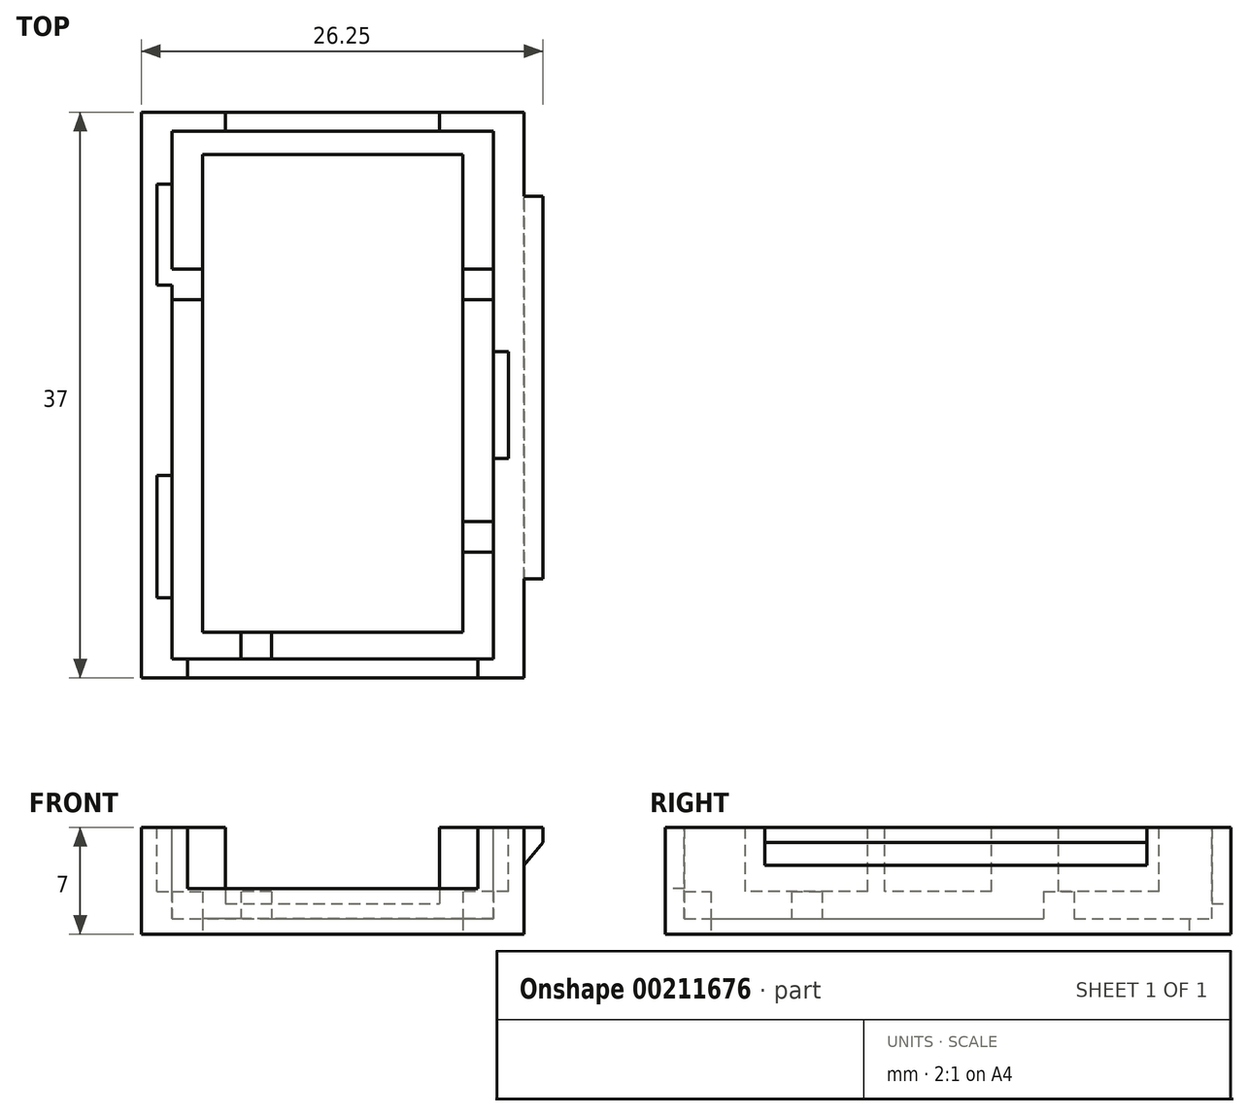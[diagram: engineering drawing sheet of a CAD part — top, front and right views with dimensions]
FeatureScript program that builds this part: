
annotation { "Feature Type Name" : "Feature", "Feature Type Description" : "" }
export const myFeature = defineFeature(function(context is Context, id is Id, definition is map)
    precondition{}
    {
        {
            var Q0;
            Q0=qCreatedBy(makeId("Top.planeOp"),FACE);
            var sketch = newSketch(context, id + "F0", { "sketchPlane" : qUnion([Q0])});
            skLineSegment(sketch, "E0", {"start": v(0, 0) * mm, "end": v(65.42, 0) * mm, "construction": true});
            skLineSegment(sketch, "E1", {"start": v(0, 0) * mm, "end": v(0, 57) * mm, "construction": true});
            skLineSegment(sketch, "E2.bottom", {"start": v(11, 17.5) * mm, "end": v(-11, 17.5) * mm, "construction": true});
            skLineSegment(sketch, "E2.top", {"start": v(11, -17.5) * mm, "end": v(-11, -17.5) * mm, "construction": true});
            skLineSegment(sketch, "E2.left", {"start": v(11, 17.5) * mm, "end": v(11, -17.5) * mm, "construction": true});
            skLineSegment(sketch, "E2.right", {"start": v(-11, 17.5) * mm, "end": v(-11, -17.5) * mm, "construction": true});
            skPoint(sketch, "E2.middle", {"position": v(0, 0) * mm});
            skPoint(sketch, "E3.orphan", {"position": v(0, -17.5) * mm});
            skLineSegment(sketch, "E4.bottom", {"start": v(12.5, 19) * mm, "end": v(-12.5, 19) * mm});
            skLineSegment(sketch, "E4.top", {"start": v(12.5, -19) * mm, "end": v(-12.5, -19) * mm});
            skLineSegment(sketch, "E4.left", {"start": v(12.5, 19) * mm, "end": v(12.5, -19) * mm});
            skLineSegment(sketch, "E4.right", {"start": v(-12.5, 19) * mm, "end": v(-12.5, -19) * mm});
            skSolve(sketch);
        }
        {
            var Q0;
            Q0=makeQuery(id+"F0.imprint","IMPRINT",FACE,{"disambiguationData":[TD([[makeQuery(id+"F0.imprint","IMPRINT",EDGE,{"derivedFrom":sQuery(id+"F0.wireOp",EDGE,"E4.bottom")}),1.0]])]});
            extrude(context, id + "F1", {"entities" : qUnion([Q0]), "depth" : 7 * mm});
        }
        {
            var Q0;
            Q0=makeQuery(id+"F1.opExtrude","CAP_FACE",FACE,{"disambiguationData":[OSD([sQuery(id+"F0.wireOp",EDGE,"E4.bottom"),sQuery(id+"F0.wireOp",EDGE,"E4.top"),sQuery(id+"F0.wireOp",EDGE,"E4.left"),sQuery(id+"F0.wireOp",EDGE,"E4.right")])],"isStart":false});
            var sketch = newSketch(context, id + "F2", { "sketchPlane" : qUnion([Q0])});
            skLineSegment(sketch, "E5.bottom", {"start": v(-10.5, -17.75) * mm, "end": v(10.5, -17.75) * mm});
            skLineSegment(sketch, "E5.top", {"start": v(-10.5, 16.75) * mm, "end": v(10.5, 16.75) * mm});
            skLineSegment(sketch, "E5.left", {"start": v(-10.5, -17.75) * mm, "end": v(-10.5, 16.75) * mm});
            skLineSegment(sketch, "E5.right", {"start": v(10.5, -17.75) * mm, "end": v(10.5, 16.75) * mm});
            skSolve(sketch);
        }
        {
            var Q0;
            Q0=qSketchRegion(id+"F2",true);
            extrude(context, id + "F3", {"entities" : qUnion([Q0]), "operationType" : NewBodyOperationType.REMOVE, "oppositeDirection" : true, "depth" : 6 * mm});
        }
        {
            var Q0;
            Q0=makeQuery(id+"F3.boolean.opBoolean","COPY",FACE,{"derivedFrom":makeQuery(id+"F3.opExtrude","CAP_FACE",FACE,{"disambiguationData":[OSD([sQuery(id+"F2.wireOp",EDGE,"E5.bottom"),sQuery(id+"F2.wireOp",EDGE,"E5.top"),sQuery(id+"F2.wireOp",EDGE,"E5.left"),sQuery(id+"F2.wireOp",EDGE,"E5.right")])],"isStart":false})});
            var sketch = newSketch(context, id + "F4", { "sketchPlane" : qUnion([Q0])});
            skLineSegment(sketch, "E6.bottom", {"start": v(-10.5, 5.75) * mm, "end": v(-8.5, 5.75) * mm});
            skLineSegment(sketch, "E6.top", {"start": v(-10.5, 7.75) * mm, "end": v(-8.5, 7.75) * mm});
            skLineSegment(sketch, "E6.left", {"start": v(-10.5, 7.75) * mm, "end": v(-10.5, 5.75) * mm});
            skLineSegment(sketch, "E6.right", {"start": v(-8.5, 7.75) * mm, "end": v(-8.5, 5.75) * mm});
            skLineSegment(sketch, "E7.MirrorCS", {"start": v(10.5, 5.75) * mm, "end": v(8.5, 5.75) * mm});
            skLineSegment(sketch, "E8.MirrorCS", {"start": v(8.5, 7.75) * mm, "end": v(8.5, 5.75) * mm});
            skLineSegment(sketch, "E9.MirrorCS", {"start": v(10.5, 7.75) * mm, "end": v(8.5, 7.75) * mm});
            skLineSegment(sketch, "E10.MirrorCS", {"start": v(10.5, 7.75) * mm, "end": v(10.5, 5.75) * mm});
            skLineSegment(sketch, "E11.bottom", {"start": v(10.5, -10.75) * mm, "end": v(8.5, -10.75) * mm});
            skLineSegment(sketch, "E11.top", {"start": v(10.5, -8.75) * mm, "end": v(8.5, -8.75) * mm});
            skLineSegment(sketch, "E11.left", {"start": v(10.5, -10.75) * mm, "end": v(10.5, -8.75) * mm});
            skLineSegment(sketch, "E11.right", {"start": v(8.5, -10.75) * mm, "end": v(8.5, -8.75) * mm});
            skLineSegment(sketch, "E12.bottom", {"start": v(-6, -18) * mm, "end": v(-4, -18) * mm});
            skLineSegment(sketch, "E12.top", {"start": v(-6, -16) * mm, "end": v(-4, -16) * mm});
            skLineSegment(sketch, "E12.left", {"start": v(-6, -18) * mm, "end": v(-6, -16) * mm});
            skLineSegment(sketch, "E12.right", {"start": v(-4, -18) * mm, "end": v(-4, -16) * mm});
            skSolve(sketch);
        }
        {
            var Q0;
            Q0=qSketchRegion(id+"F4",true);
            extrude(context, id + "F5", {"entities" : qUnion([Q0]), "operationType" : NewBodyOperationType.ADD, "depth" : 1.8 * mm});
        }
        {
            var Q0;
            Q0=qCreatedBy(makeId("Top.planeOp"),FACE);
            var sketch = newSketch(context, id + "F6", { "sketchPlane" : qUnion([Q0])});
            skLineSegment(sketch, "E13.bottom", {"start": v(-8.5, 15.25) * mm, "end": v(8.5, 15.25) * mm});
            skLineSegment(sketch, "E13.left", {"start": v(-8.5, 15.25) * mm, "end": v(-8.5, -16) * mm});
            skLineSegment(sketch, "E14.top", {"start": v(-8.5, -16) * mm, "end": v(8.5, -16) * mm});
            skLineSegment(sketch, "E14.right", {"start": v(8.5, 15.25) * mm, "end": v(8.5, -16) * mm});
            skSolve(sketch);
        }
        {
            var Q0;
            Q0=qSketchRegion(id+"F6",true);
            extrude(context, id + "F7", {"entities" : qUnion([Q0]), "operationType" : NewBodyOperationType.REMOVE, "endBound" : BoundingType.THROUGH_ALL, "depth" : 25 * mm});
        }
        {
            var Q0;
            Q0=makeQuery(id+"F1.opExtrude","CAP_FACE",FACE,{"disambiguationData":[OSD([sQuery(id+"F0.wireOp",EDGE,"E4.bottom"),sQuery(id+"F0.wireOp",EDGE,"E4.top"),sQuery(id+"F0.wireOp",EDGE,"E4.left"),sQuery(id+"F0.wireOp",EDGE,"E4.right")])],"isStart":false});
            var sketch = newSketch(context, id + "F8", { "sketchPlane" : qUnion([Q0])});
            skLineSegment(sketch, "E15.bottom", {"start": v(-10.47, 6.7) * mm, "end": v(-11.47, 6.7) * mm});
            skLineSegment(sketch, "E15.top", {"start": v(-10.47, 13.3) * mm, "end": v(-11.47, 13.3) * mm});
            skLineSegment(sketch, "E15.left", {"start": v(-10.47, 6.7) * mm, "end": v(-10.47, 13.3) * mm});
            skLineSegment(sketch, "E15.right", {"start": v(-11.47, 6.7) * mm, "end": v(-11.47, 13.3) * mm});
            skLineSegment(sketch, "E16.bottom", {"start": v(10.5, 2.35) * mm, "end": v(11.5, 2.35) * mm});
            skLineSegment(sketch, "E16.top", {"start": v(10.5, -4.65) * mm, "end": v(11.5, -4.65) * mm});
            skLineSegment(sketch, "E16.left", {"start": v(10.5, 2.35) * mm, "end": v(10.5, -4.65) * mm});
            skLineSegment(sketch, "E16.right", {"start": v(11.5, 2.35) * mm, "end": v(11.5, -4.65) * mm});
            skLineSegment(sketch, "E17.bottom", {"start": v(-10.5, -13.75) * mm, "end": v(-11.47, -13.75) * mm});
            skLineSegment(sketch, "E17.top", {"start": v(-10.5, -5.75) * mm, "end": v(-11.47, -5.75) * mm});
            skLineSegment(sketch, "E17.left", {"start": v(-10.5, -13.75) * mm, "end": v(-10.5, -5.75) * mm});
            skLineSegment(sketch, "E17.right", {"start": v(-11.47, -13.75) * mm, "end": v(-11.47, -5.75) * mm});
            skSolve(sketch);
        }
        {
            var Q0;
            {var subQ0=sQuery(id+"F8.wireOp",EDGE,"E15.bottom");Q0=makeQuery(id+"F8.imprint","IMPRINT",FACE,{"disambiguationData":[TD([[makeQuery(id+"F8.imprint","IMPRINT",EDGE,{"derivedFrom":subQ0}),-1.0]])]});}
            var Q1;
            {var subQ0=sQuery(id+"F8.wireOp",EDGE,"E15.top");Q1=makeQuery(id+"F8.imprint","IMPRINT",FACE,{"disambiguationData":[TD([[makeQuery(id+"F8.imprint","IMPRINT",EDGE,{"derivedFrom":subQ0}),1.0]])]});}
            var Q2;
            Q2=makeQuery(id+"F8.imprint","IMPRINT",FACE,{"disambiguationData":[TD([[makeQuery(id+"F8.imprint","IMPRINT",EDGE,{"derivedFrom":sQuery(id+"F8.wireOp",EDGE,"E16.bottom")}),-1.0]])]});
            var Q3;
            {var subQ0=sQuery(id+"F8.wireOp",EDGE,"lNjhLBkX-aFZr-f505-E5Ee-j5UPzdD6XMNG.bottom");Q3=makeQuery(id+"F8.imprint","IMPRINT",FACE,{"disambiguationData":[TD([[makeQuery(id+"F8.imprint","IMPRINT",EDGE,{"derivedFrom":subQ0}),1.0]])]});}
            var Q4;
            {var subQ0=sQuery(id+"F8.wireOp",EDGE,"lNjhLBkX-aFZr-f505-E5Ee-j5UPzdD6XMNG.top");Q4=makeQuery(id+"F8.imprint","IMPRINT",FACE,{"disambiguationData":[TD([[makeQuery(id+"F8.imprint","IMPRINT",EDGE,{"derivedFrom":subQ0}),-1.0]])]});}
            var Q5;
            Q5=makeQuery(id+"F8.imprint","IMPRINT",FACE,{"disambiguationData":[TD([[makeQuery(id+"F8.imprint","IMPRINT",EDGE,{"derivedFrom":sQuery(id+"F8.wireOp",EDGE,"E17.bottom")}),-1.0]])]});
            var Q6;
            Q6=makeQuery(id+"F5.opExtrude","CAP_FACE",FACE,{"disambiguationData":[OSD([sQuery(id+"F4.wireOp",EDGE,"E6.bottom"),sQuery(id+"F4.wireOp",EDGE,"E6.top"),sQuery(id+"F4.wireOp",EDGE,"E6.left"),sQuery(id+"F4.wireOp",EDGE,"E6.right")])],"isStart":false});
            extrude(context, id + "F9", {"entities" : qUnion([Q0, Q1, Q2, Q3, Q4, Q5]), "operationType" : NewBodyOperationType.REMOVE, "endBound" : BoundingType.UP_TO_SURFACE, "oppositeDirection" : true, "endBoundEntityFace" : qUnion([Q6]), "depth" : 3 * mm});
        }
        {
            var Q0;
            {var subQ10=sQuery(id+"F4.wireOp",EDGE,"E6.bottom");Q0=makeQuery(id+"F4.imprint","IMPRINT",FACE,{"disambiguationData":[TD([[makeQuery(id+"F4.imprint","IMPRINT",EDGE,{"derivedFrom":subQ10}),-1.0]])]});}
            cPlane(context, id + "F10", {"entities" : qUnion([Q0]), "cplaneType" : CPlaneType.OFFSET, "offset" : 1 * mm, "width" : 150 * mm, "height" : 150 * mm});
        }
        {
            var Q0;
            Q0=qCreatedBy(id+"F10.planeOp",FACE);
            var sketch = newSketch(context, id + "F11", { "sketchPlane" : qUnion([Q0])});
            skLineSegment(sketch, "E18.bottom", {"start": v(-7, 16.75) * mm, "end": v(7, 16.75) * mm});
            skLineSegment(sketch, "E18.top", {"start": v(-7, 21.75) * mm, "end": v(7, 21.75) * mm});
            skLineSegment(sketch, "E18.left", {"start": v(-7, 16.75) * mm, "end": v(-7, 21.75) * mm});
            skLineSegment(sketch, "E18.right", {"start": v(7, 16.75) * mm, "end": v(7, 21.75) * mm});
            skSolve(sketch);
        }
        {
            var Q0;
            {var subQ0=sQuery(id+"F11.wireOp",EDGE,"E18.top");Q0=makeQuery(id+"F11.imprint","IMPRINT",FACE,{"disambiguationData":[TD([[makeQuery(id+"F11.imprint","IMPRINT",EDGE,{"derivedFrom":subQ0}),-1.0]])]});}
            var Q1;
            {var subQ0=sQuery(id+"F11.wireOp",EDGE,"E18.bottom");Q1=makeQuery(id+"F11.imprint","IMPRINT",FACE,{"disambiguationData":[TD([[makeQuery(id+"F11.imprint","IMPRINT",EDGE,{"derivedFrom":subQ0}),1.0]])]});}
            extrude(context, id + "F12", {"entities" : qUnion([Q0, Q1]), "operationType" : NewBodyOperationType.REMOVE, "depth" : 5 * mm});
        }
        {
            var Q0;
            Q0=makeQuery(id+"F1.opExtrude","SWEPT_FACE",FACE,{"disambiguationData":[OSD([sQuery(id+"F0.wireOp",EDGE,"E4.bottom")])]});
            extrude(context, id + "F13", {"entities" : qUnion([Q0]), "operationType" : NewBodyOperationType.REMOVE, "oppositeDirection" : true, "depth" : 1 * mm});
        }
        {
            var Q0;
            Q0=qCreatedBy(makeId("Front.planeOp"),FACE);
            var sketch = newSketch(context, id + "F14", { "sketchPlane" : qUnion([Q0])});
            skLineSegment(sketch, "E19", {"start": v(12.5, 7) * mm, "end": v(13.75, 7) * mm});
            skLineSegment(sketch, "E20", {"start": v(13.75, 7) * mm, "end": v(13.75, 6) * mm});
            skLineSegment(sketch, "E21", {"start": v(13.75, 6) * mm, "end": v(12.5, 4.51) * mm});
            skLineSegment(sketch, "E22", {"start": v(12.5, 4.51) * mm, "end": v(12.5, 7) * mm});
            skSolve(sketch);
        }
        {
            var Q0;
            Q0=makeQuery(id+"F14.imprint","IMPRINT",FACE,{"disambiguationData":[TD([[makeQuery(id+"F14.imprint","IMPRINT",EDGE,{"derivedFrom":sQuery(id+"F14.wireOp",EDGE,"E19")}),-1.0]])]});
            extrude(context, id + "F15", {"entities" : qUnion([Q0]), "operationType" : NewBodyOperationType.ADD, "endBound" : BoundingType.SYMMETRIC, "depth" : 25 * mm});
        }
        {
            var Q0;
            Q0=makeQuery(id+"F1.opExtrude","SWEPT_FACE",FACE,{"disambiguationData":[OSD([sQuery(id+"F0.wireOp",EDGE,"E4.top")])]});
            var sketch = newSketch(context, id + "F16", { "sketchPlane" : qUnion([Q0])});
            skLineSegment(sketch, "E23.bottom", {"start": v(-9.5, 7) * mm, "end": v(9.5, 7) * mm});
            skLineSegment(sketch, "E23.top", {"start": v(-9.5, 3) * mm, "end": v(9.5, 3) * mm});
            skLineSegment(sketch, "E23.left", {"start": v(-9.5, 7) * mm, "end": v(-9.5, 3) * mm});
            skLineSegment(sketch, "E23.right", {"start": v(9.5, 7) * mm, "end": v(9.5, 3) * mm});
            skSolve(sketch);
        }
        {
            var Q0;
            Q0=makeQuery(id+"F16.imprint","IMPRINT",FACE,{"disambiguationData":[TD([[makeQuery(id+"F16.imprint","IMPRINT",EDGE,{"derivedFrom":sQuery(id+"F16.wireOp",EDGE,"E23.bottom")}),1.0]])]});
            extrude(context, id + "F17", {"entities" : qUnion([Q0]), "operationType" : NewBodyOperationType.REMOVE, "oppositeDirection" : true, "depth" : 3 * mm});
        }
    });
